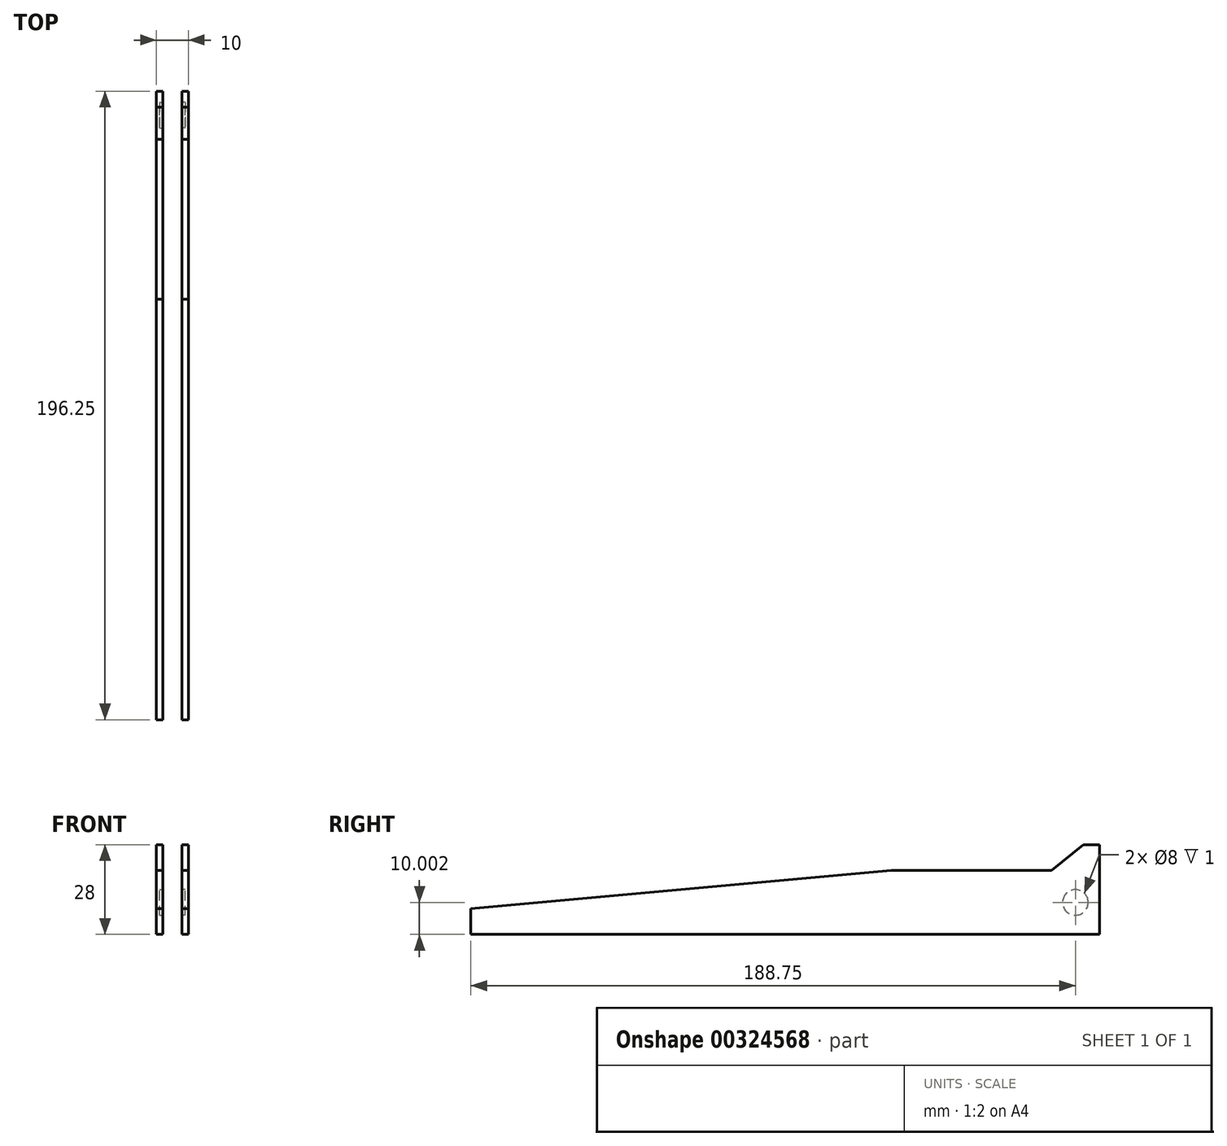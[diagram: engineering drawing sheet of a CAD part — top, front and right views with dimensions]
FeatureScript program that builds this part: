
annotation { "Feature Type Name" : "Feature", "Feature Type Description" : "" }
export const myFeature = defineFeature(function(context is Context, id is Id, definition is map)
    precondition{}
    {
        {
            var Q0;
            Q0=qCreatedBy(makeId("Right.planeOp"),FACE);
            var sketch = newSketch(context, id + "F0", { "sketchPlane" : qUnion([Q0])});
            skLineSegment(sketch, "E0", {"start": v(-118.41, -16.39) * mm, "end": v(-118.41, -8.39) * mm});
            skLineSegment(sketch, "E1", {"start": v(-118.41, -8.39) * mm, "end": v(12.84, 3.61) * mm});
            skLineSegment(sketch, "E2", {"start": v(12.84, 3.61) * mm, "end": v(77.84, 3.61) * mm});
            skLineSegment(sketch, "E3", {"start": v(77.84, -16.39) * mm, "end": v(77.84, 3.61) * mm});
            skLineSegment(sketch, "E4", {"start": v(-118.41, -16.39) * mm, "end": v(77.84, -16.39) * mm});
            skLineSegment(sketch, "E5", {"start": v(77.84, 3.61) * mm, "end": v(77.84, 11.61) * mm});
            skLineSegment(sketch, "E6", {"start": v(77.84, 11.61) * mm, "end": v(72.84, 11.61) * mm});
            skLineSegment(sketch, "E7", {"start": v(72.84, 11.61) * mm, "end": v(62.84, 3.61) * mm});
            skCircle(sketch, "E8", {"center": v(70.34, -6.39) * mm, "radius": 4 * mm});
            skLineSegment(sketch, "E9", {"start": v(-114.41, -10.03) * mm, "end": v(-114.41, -14.39) * mm});
            skLineSegment(sketch, "E10", {"start": v(-114.41, -14.39) * mm, "end": v(12.93, -14.39) * mm});
            skLineSegment(sketch, "E11", {"start": v(12.93, -14.39) * mm, "end": v(12.93, 1.61) * mm});
            skLineSegment(sketch, "E12", {"start": v(12.93, 1.61) * mm, "end": v(-114.41, -10.03) * mm});
            skLineSegment(sketch, "E13.bottom", {"start": v(16.93, 1.61) * mm, "end": v(62.84, 1.61) * mm});
            skLineSegment(sketch, "E13.top", {"start": v(16.93, -14.39) * mm, "end": v(62.84, -14.39) * mm});
            skLineSegment(sketch, "E13.left", {"start": v(16.93, 1.61) * mm, "end": v(16.93, -14.39) * mm});
            skLineSegment(sketch, "E13.right", {"start": v(62.84, 1.61) * mm, "end": v(62.84, -14.39) * mm});
            skLineSegment(sketch, "E14", {"start": v(77.84, -6.39) * mm, "end": v(62.84, -6.39) * mm});
            skLineSegment(sketch, "E15", {"start": v(-118.41, -4.09) * mm, "end": v(12.84, 7.91) * mm});
            skLineSegment(sketch, "E16", {"start": v(12.84, 7.91) * mm, "end": v(62.84, 7.91) * mm});
            skLineSegment(sketch, "E17", {"start": v(62.84, 7.91) * mm, "end": v(64.1, 8.91) * mm});
            skLineSegment(sketch, "E18", {"start": v(64.1, 8.91) * mm, "end": v(12.8, 8.91) * mm});
            skLineSegment(sketch, "E19", {"start": v(12.8, 8.91) * mm, "end": v(-118.41, -3.08) * mm});
            skLineSegment(sketch, "E20", {"start": v(-118.41, -3.08) * mm, "end": v(-118.41, -4.09) * mm});
            skSolve(sketch);
        }
        {
            var Q0;
            Q0=makeQuery(id+"F0.imprint","IMPRINT",FACE,{"disambiguationData":[TD([[makeQuery(id+"F0.imprint","IMPRINT",EDGE,{"derivedFrom":sQuery(id+"F0.wireOp",EDGE,"E0")}),-1.0]])]});
            var Q1;
            Q1=makeQuery(id+"F0.imprint","IMPRINT",FACE,{"disambiguationData":[TD([[makeQuery(id+"F0.imprint","IMPRINT",EDGE,{"derivedFrom":sQuery(id+"F0.wireOp",EDGE,"E9")}),1.0]])]});
            var Q2;
            {var subQ1=sQuery(id+"F0.wireOp",EDGE,"E13.bottom");Q2=makeQuery(id+"F0.imprint","IMPRINT",FACE,{"disambiguationData":[TD([[makeQuery(id+"F0.imprint","IMPRINT",EDGE,{"derivedFrom":subQ1}),-1.0]])]});}
            var Q3;
            {var subQ0=sQuery(id+"F0.wireOp",EDGE,"E14");var subQ1=sQuery(id+"F0.wireOp",EDGE,"E8");var subQ2=makeQuery(id+"F0.imprint","INTERSECT",VERTEX,{"disambiguationData":[OD(0.0)],"derivedFrom":[subQ1,subQ0]});Q3=makeQuery(id+"F0.imprint","IMPRINT",FACE,{"disambiguationData":[TD([[makeQuery(id+"F0.imprint","IMPRINT",EDGE,{"disambiguationData":[TD([[subQ2,-1.0]])],"derivedFrom":subQ1}),1.0]])]});}
            var Q4;
            {var subQ0=sQuery(id+"F0.wireOp",EDGE,"E14");var subQ1=sQuery(id+"F0.wireOp",EDGE,"E8");var subQ2=makeQuery(id+"F0.imprint","INTERSECT",VERTEX,{"disambiguationData":[OD(0.0)],"derivedFrom":[subQ1,subQ0]});Q4=makeQuery(id+"F0.imprint","IMPRINT",FACE,{"disambiguationData":[TD([[makeQuery(id+"F0.imprint","IMPRINT",EDGE,{"disambiguationData":[TD([[subQ2,1.0]])],"derivedFrom":subQ1}),1.0]])]});}
            var Q5;
            {var subQ0=sQuery(id+"F0.wireOp",EDGE,"E5");Q5=makeQuery(id+"F0.imprint","IMPRINT",FACE,{"disambiguationData":[TD([[makeQuery(id+"F0.imprint","IMPRINT",EDGE,{"derivedFrom":subQ0}),1.0]])]});}
            extrude(context, id + "F1", {"entities" : qUnion([Q0, Q1, Q2, Q3, Q4, Q5]), "depth" : 5 * mm, "hasSecondDirection" : true, "secondDirectionOppositeDirection" : true, "secondDirectionDepth" : -3 * mm});
        }
        {
            var Q0;
            {var subQ0=sQuery(id+"F0.wireOp",EDGE,"E14");var subQ1=sQuery(id+"F0.wireOp",EDGE,"E8");var subQ2=makeQuery(id+"F0.imprint","INTERSECT",VERTEX,{"disambiguationData":[OD(0.0)],"derivedFrom":[subQ1,subQ0]});Q0=makeQuery(id+"F0.imprint","IMPRINT",FACE,{"disambiguationData":[TD([[makeQuery(id+"F0.imprint","IMPRINT",EDGE,{"disambiguationData":[TD([[subQ2,1.0]])],"derivedFrom":subQ1}),1.0]])]});}
            var Q1;
            {var subQ0=sQuery(id+"F0.wireOp",EDGE,"E14");var subQ1=sQuery(id+"F0.wireOp",EDGE,"E8");var subQ2=makeQuery(id+"F0.imprint","INTERSECT",VERTEX,{"disambiguationData":[OD(0.0)],"derivedFrom":[subQ1,subQ0]});Q1=makeQuery(id+"F0.imprint","IMPRINT",FACE,{"disambiguationData":[TD([[makeQuery(id+"F0.imprint","IMPRINT",EDGE,{"disambiguationData":[TD([[subQ2,-1.0]])],"derivedFrom":subQ1}),1.0]])]});}
            extrude(context, id + "F2", {"entities" : qUnion([Q0, Q1]), "operationType" : NewBodyOperationType.REMOVE, "oppositeDirection" : true, "depth" : -4 * mm});
        }
        {
            var Q0;
            Q0=makeQuery(id+"F1.opExtrude","SWEPT_BODY",BODY,{"disambiguationData":[OSD([sQuery(id+"F0.wireOp",EDGE,"E0"),sQuery(id+"F0.wireOp",EDGE,"E1"),sQuery(id+"F0.wireOp",EDGE,"E2"),sQuery(id+"F0.wireOp",EDGE,"E3"),sQuery(id+"F0.wireOp",EDGE,"E4"),sQuery(id+"F0.wireOp",EDGE,"E5"),sQuery(id+"F0.wireOp",EDGE,"E6"),sQuery(id+"F0.wireOp",EDGE,"E7")])]});
            transform(context, id + "F3", {"entities" : qUnion([Q0]), "transformType" : TransformType.TRANSLATION_3D, "dx" : -100 * mm, "dy" : 0 * mm, "dz" : 0 * mm, "makeCopy" : true});
        }
        {
            var Q0;
            Q0=makeQuery(id+"F3.opPattern","COPY",BODY,{"derivedFrom":makeQuery(id+"F1.opExtrude","SWEPT_BODY",BODY,{"disambiguationData":[OSD([sQuery(id+"F0.wireOp",EDGE,"E0"),sQuery(id+"F0.wireOp",EDGE,"E1"),sQuery(id+"F0.wireOp",EDGE,"E2"),sQuery(id+"F0.wireOp",EDGE,"E3"),sQuery(id+"F0.wireOp",EDGE,"E4"),sQuery(id+"F0.wireOp",EDGE,"E5"),sQuery(id+"F0.wireOp",EDGE,"E6"),sQuery(id+"F0.wireOp",EDGE,"E7")])]}),"instanceName":"1"});
            deleteBodies(context, id + "F4", {"entities" : qUnion([Q0])});
        }
        {
            var Q0;
            Q0=makeQuery(id+"F1.opExtrude","SWEPT_BODY",BODY,{"disambiguationData":[OSD([sQuery(id+"F0.wireOp",EDGE,"E0"),sQuery(id+"F0.wireOp",EDGE,"E1"),sQuery(id+"F0.wireOp",EDGE,"E2"),sQuery(id+"F0.wireOp",EDGE,"E3"),sQuery(id+"F0.wireOp",EDGE,"E4"),sQuery(id+"F0.wireOp",EDGE,"E5"),sQuery(id+"F0.wireOp",EDGE,"E6"),sQuery(id+"F0.wireOp",EDGE,"E7")])]});
            var Q1;
            Q1=qCreatedBy(makeId("Right.planeOp"),FACE);
            mirror(context, id + "F5", {"entities" : qUnion([Q0]), "mirrorPlane" : qUnion([Q1])});
        }
    });
